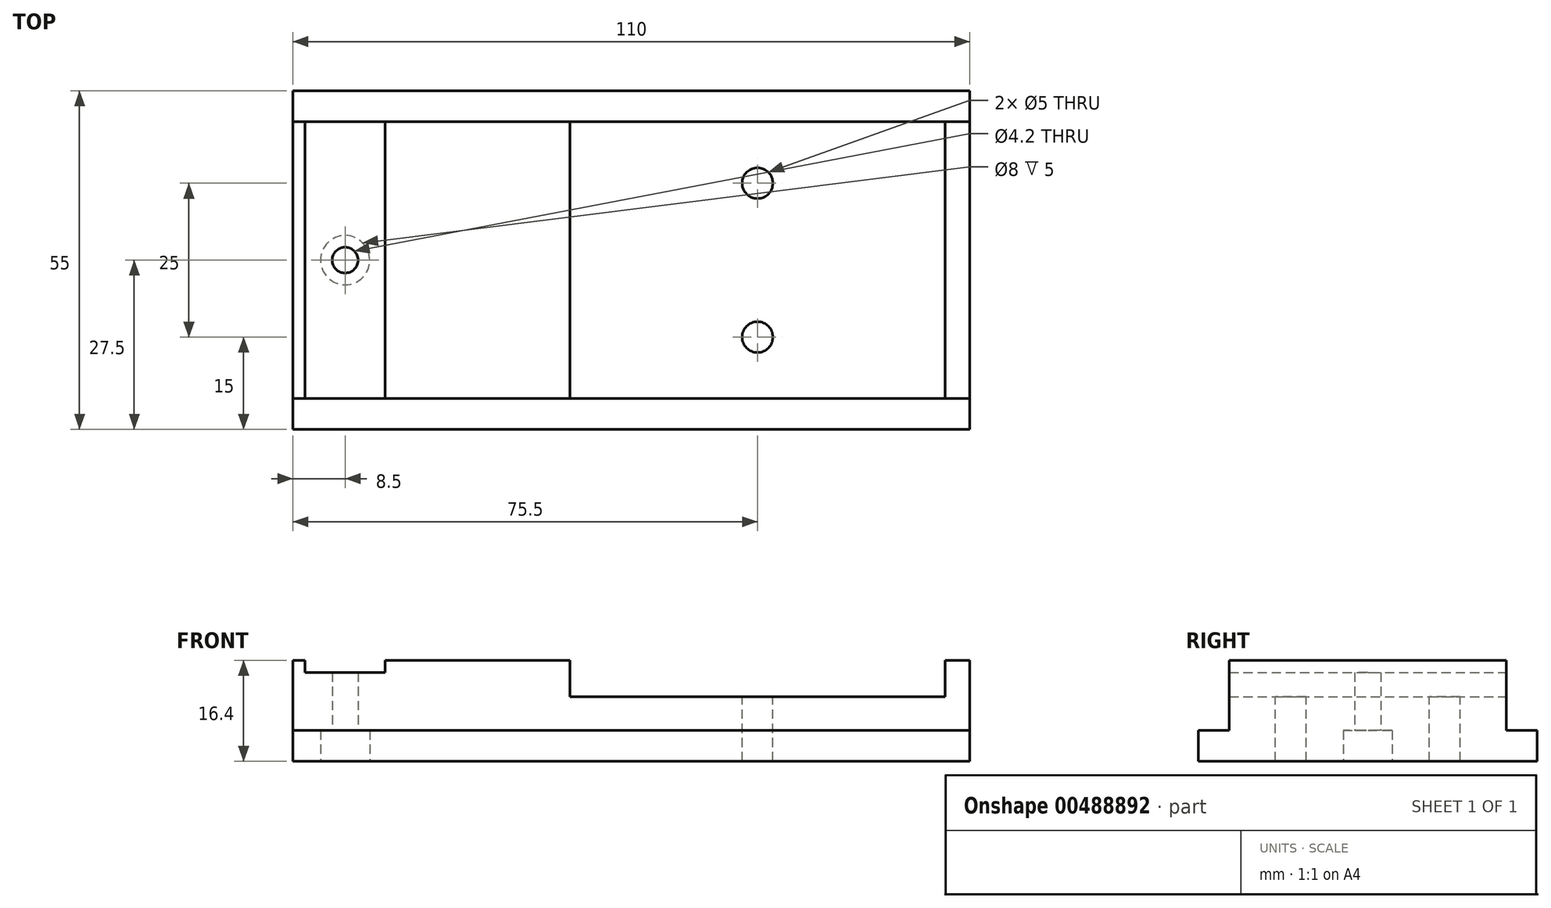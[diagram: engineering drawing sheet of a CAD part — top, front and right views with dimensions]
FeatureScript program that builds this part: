
annotation { "Feature Type Name" : "Feature", "Feature Type Description" : "" }
export const myFeature = defineFeature(function(context is Context, id is Id, definition is map)
    precondition{}
    {
        {
            var Q0;
            Q0=qCreatedBy(makeId("Top.planeOp"),FACE);
            var sketch = newSketch(context, id + "F0", { "sketchPlane" : qUnion([Q0])});
            skLineSegment(sketch, "E0.bottom", {"start": v(55, 27.5) * mm, "end": v(-55, 27.5) * mm});
            skLineSegment(sketch, "E0.top", {"start": v(55, -27.5) * mm, "end": v(-55, -27.5) * mm});
            skLineSegment(sketch, "E0.left", {"start": v(55, 27.5) * mm, "end": v(55, -27.5) * mm});
            skLineSegment(sketch, "E0.right", {"start": v(-55, 27.5) * mm, "end": v(-55, -27.5) * mm});
            skPoint(sketch, "E0.middle", {"position": v(0, 0) * mm});
            skSolve(sketch);
        }
        {
            var Q0;
            Q0=qSketchRegion(id+"F0",true);
            extrude(context, id + "F1", {"entities" : qUnion([Q0]), "depth" : 5 * mm});
        }
        {
            var Q0;
            Q0=makeQuery(id+"F1.opExtrude","CAP_FACE",FACE,{"disambiguationData":[OSD([sQuery(id+"F0.wireOp",EDGE,"E0.bottom"),sQuery(id+"F0.wireOp",EDGE,"E0.top"),sQuery(id+"F0.wireOp",EDGE,"E0.left"),sQuery(id+"F0.wireOp",EDGE,"E0.right")])],"isStart":false});
            var sketch = newSketch(context, id + "F2", { "sketchPlane" : qUnion([Q0])});
            skLineSegment(sketch, "E1.bottom", {"start": v(55, 22.5) * mm, "end": v(-55, 22.5) * mm});
            skLineSegment(sketch, "E1.top", {"start": v(55, -22.5) * mm, "end": v(-55, -22.5) * mm});
            skLineSegment(sketch, "E1.left", {"start": v(55, 22.5) * mm, "end": v(55, -22.5) * mm});
            skLineSegment(sketch, "E1.right", {"start": v(-55, 22.5) * mm, "end": v(-55, -22.5) * mm});
            skPoint(sketch, "E1.middle", {"position": v(0, 0) * mm});
            skSolve(sketch);
        }
        {
            var Q0;
            Q0=makeQuery(id+"F2.imprint","IMPRINT",FACE,{"disambiguationData":[TD([[makeQuery(id+"F2.imprint","IMPRINT",EDGE,{"derivedFrom":sQuery(id+"F2.wireOp",EDGE,"E1.bottom")}),1.0]])]});
            extrude(context, id + "F3", {"entities" : qUnion([Q0]), "operationType" : NewBodyOperationType.ADD, "depth" : 11.4 * mm});
        }
        {
            var Q0;
            Q0=makeQuery(id+"F3.opExtrude","CAP_FACE",FACE,{"disambiguationData":[OSD([sQuery(id+"F2.wireOp",EDGE,"E1.bottom"),sQuery(id+"F2.wireOp",EDGE,"E1.top"),sQuery(id+"F2.wireOp",EDGE,"E1.left"),sQuery(id+"F2.wireOp",EDGE,"E1.right")])],"isStart":false});
            var sketch = newSketch(context, id + "F4", { "sketchPlane" : qUnion([Q0])});
            skLineSegment(sketch, "E2.bottom", {"start": v(-55, -22.5) * mm, "end": v(-53, -22.5) * mm});
            skLineSegment(sketch, "E2.top", {"start": v(-55, 22.5) * mm, "end": v(-53, 22.5) * mm});
            skLineSegment(sketch, "E2.left", {"start": v(-55, -22.5) * mm, "end": v(-55, 22.5) * mm});
            skLineSegment(sketch, "E2.right", {"start": v(-53, -22.5) * mm, "end": v(-53, 22.5) * mm});
            skLineSegment(sketch, "E3.bottom", {"start": v(-53, -22.5) * mm, "end": v(-40, -22.5) * mm});
            skLineSegment(sketch, "E3.top", {"start": v(-53, 22.5) * mm, "end": v(-40, 22.5) * mm});
            skLineSegment(sketch, "E3.right", {"start": v(-40, -22.5) * mm, "end": v(-40, 22.5) * mm});
            skLineSegment(sketch, "E4.bottom", {"start": v(-40, -22.5) * mm, "end": v(-10, -22.5) * mm});
            skLineSegment(sketch, "E4.top", {"start": v(-40, 22.5) * mm, "end": v(-10, 22.5) * mm});
            skLineSegment(sketch, "E4.right", {"start": v(-10, -22.5) * mm, "end": v(-10, 22.5) * mm});
            skLineSegment(sketch, "E5.bottom", {"start": v(-10, -22.5) * mm, "end": v(51, -22.5) * mm});
            skLineSegment(sketch, "E5.top", {"start": v(-10, 22.5) * mm, "end": v(51, 22.5) * mm});
            skLineSegment(sketch, "E5.right", {"start": v(51, -22.5) * mm, "end": v(51, 22.5) * mm});
            skSolve(sketch);
        }
        {
            var Q0;
            Q0=makeQuery(id+"F4.imprint","IMPRINT",FACE,{"disambiguationData":[TD([[makeQuery(id+"F4.imprint","IMPRINT",EDGE,{"derivedFrom":sQuery(id+"F4.wireOp",EDGE,"E3.bottom")}),-1.0]])]});
            extrude(context, id + "F5", {"entities" : qUnion([Q0]), "operationType" : NewBodyOperationType.REMOVE, "oppositeDirection" : true, "depth" : 2 * mm});
        }
        {
            var Q0;
            Q0=makeQuery(id+"F4.imprint","IMPRINT",FACE,{"disambiguationData":[TD([[makeQuery(id+"F4.imprint","IMPRINT",EDGE,{"derivedFrom":sQuery(id+"F4.wireOp",EDGE,"E5.bottom")}),-1.0]])]});
            extrude(context, id + "F6", {"entities" : qUnion([Q0]), "operationType" : NewBodyOperationType.REMOVE, "oppositeDirection" : true, "depth" : 5.9 * mm});
        }
        {
            var Q0;
            Q0=makeQuery(id+"F1.opExtrude","CAP_FACE",FACE,{"disambiguationData":[OSD([sQuery(id+"F0.wireOp",EDGE,"E0.bottom"),sQuery(id+"F0.wireOp",EDGE,"E0.top"),sQuery(id+"F0.wireOp",EDGE,"E0.left"),sQuery(id+"F0.wireOp",EDGE,"E0.right")])],"isStart":true});
            var sketch = newSketch(context, id + "F7", { "sketchPlane" : qUnion([Q0])});
            skLineSegment(sketch, "E6", {"start": v(-55, 0) * mm, "end": v(-53, 0) * mm});
            skPoint(sketch, "E6.endSnap0", {"position": v(-55, 0) * mm});
            skLineSegment(sketch, "E7", {"start": v(-53, 0) * mm, "end": v(-40, 0) * mm});
            skPoint(sketch, "E8", {"position": v(-46.5, 0) * mm});
            skSolve(sketch);
        }
        {
            var Q0;
            Q0=sQuery(id+"F7.wireOp",VERTEX,"E8");
            var Q1;
            Q1=makeQuery(id+"F1.opExtrude","SWEPT_BODY",BODY,{"disambiguationData":[OSD([sQuery(id+"F0.wireOp",EDGE,"E0.bottom"),sQuery(id+"F0.wireOp",EDGE,"E0.top"),sQuery(id+"F0.wireOp",EDGE,"E0.left"),sQuery(id+"F0.wireOp",EDGE,"E0.right")])]});
            hole(context, id + "F8", {"style" : HoleStyle.C_BORE, "endStyle" : HoleEndStyle.THROUGH, "holeDiameter" : 4.2 * mm, "cBoreDiameter" : 8 * mm, "cBoreDepth" : 5 * mm, "isTappedThrough" : true, "tappedDepth" : 12 * mm, "tapClearance" : 3, "locations" : qUnion([Q0]), "scope" : qUnion([Q1])});
        }
        {
            var Q0;
            Q0=makeQuery(id+"F6.boolean.opBoolean","COPY",FACE,{"derivedFrom":makeQuery(id+"F6.opExtrude","CAP_FACE",FACE,{"disambiguationData":[OSD([sQuery(id+"F4.wireOp",EDGE,"E5.bottom"),sQuery(id+"F4.wireOp",EDGE,"E5.top"),sQuery(id+"F4.wireOp",EDGE,"E4.right"),sQuery(id+"F4.wireOp",EDGE,"E5.right")])],"isStart":false})});
            var sketch = newSketch(context, id + "F9", { "sketchPlane" : qUnion([Q0])});
            skPoint(sketch, "E9", {"position": v(20.5, 22.5) * mm});
            skLineSegment(sketch, "E10", {"start": v(20.5, 22.5) * mm, "end": v(20.5, 12.5) * mm});
            skLineSegment(sketch, "E11", {"start": v(20.5, 12.5) * mm, "end": v(20.5, 0) * mm});
            skLineSegment(sketch, "E12", {"start": v(20.5, 0) * mm, "end": v(20.5, -12.5) * mm});
            skLineSegment(sketch, "E13", {"start": v(20.5, -12.5) * mm, "end": v(20.5, -22.5) * mm});
            skSolve(sketch);
        }
        {
            var Q0;
            Q0=sQuery(id+"F9.wireOp",VERTEX,"E11.start");
            var Q1;
            Q1=sQuery(id+"F9.wireOp",VERTEX,"E13.start");
            var Q2;
            Q2=makeQuery(id+"F1.opExtrude","SWEPT_BODY",BODY,{"disambiguationData":[OSD([sQuery(id+"F0.wireOp",EDGE,"E0.bottom"),sQuery(id+"F0.wireOp",EDGE,"E0.top"),sQuery(id+"F0.wireOp",EDGE,"E0.left"),sQuery(id+"F0.wireOp",EDGE,"E0.right")])]});
            hole(context, id + "F10", {"style" : HoleStyle.SIMPLE, "endStyle" : HoleEndStyle.THROUGH, "standardTappedOrClearance" : lookupTablePath({ "standard" : "Benutzerdefiniert" }), "standardBlindInLast" : lookupTablePath({ "standard" : "Benutzerdefiniert" }), "holeDiameter" : 5 * mm, "isTappedThrough" : true, "tappedDepth" : 12 * mm, "tapClearance" : 3, "locations" : qUnion([Q0, Q1]), "scope" : qUnion([Q2])});
        }
    });
